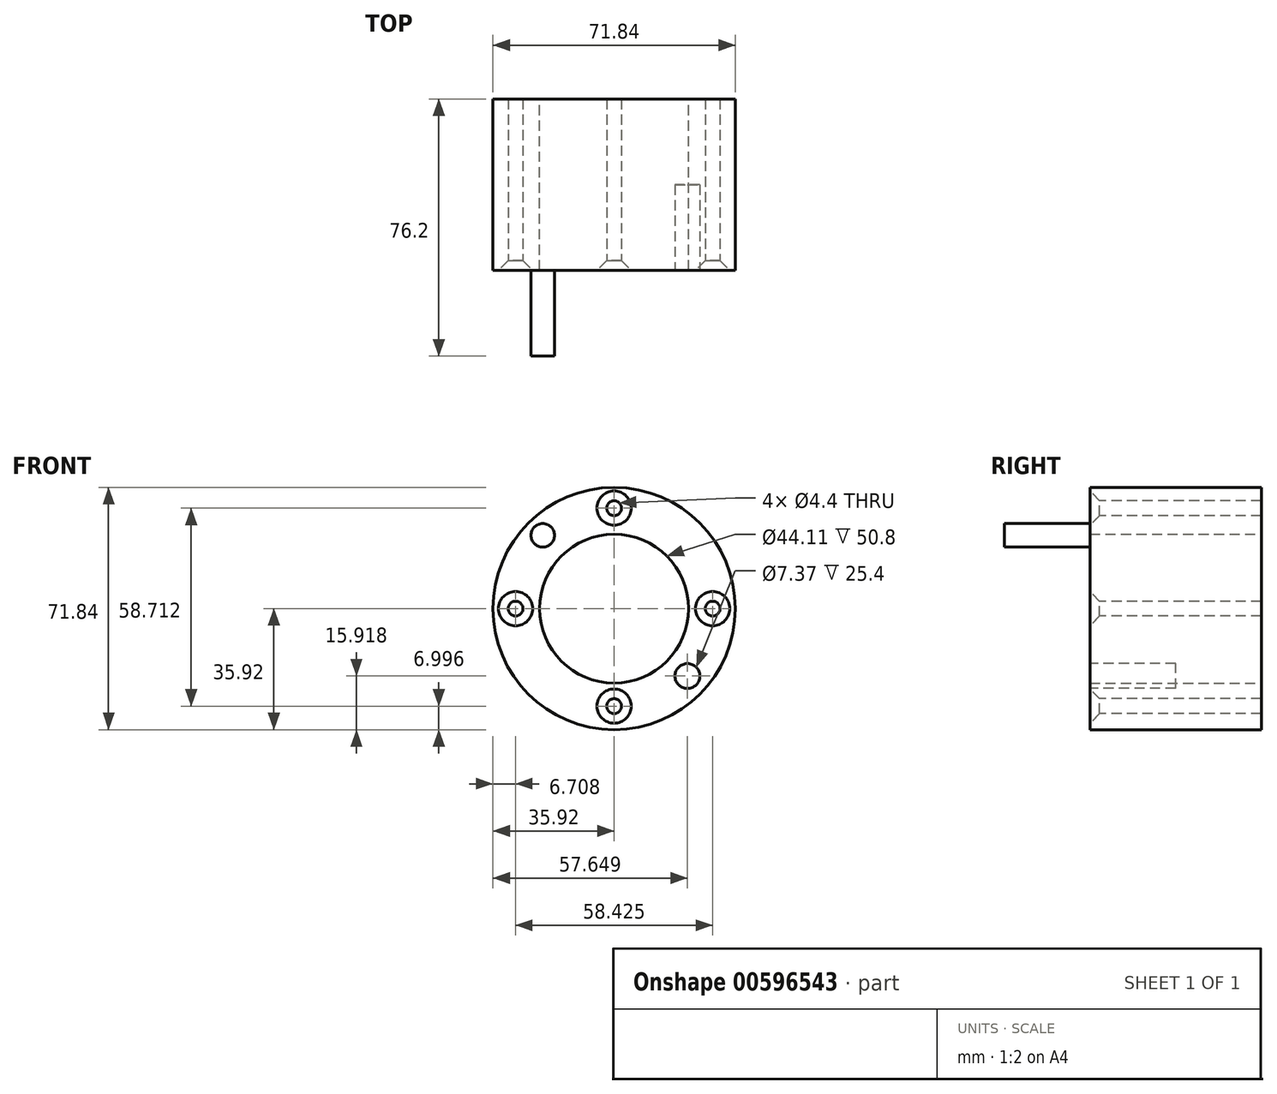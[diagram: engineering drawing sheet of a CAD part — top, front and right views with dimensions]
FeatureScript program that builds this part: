
annotation { "Feature Type Name" : "Feature", "Feature Type Description" : "" }
export const myFeature = defineFeature(function(context is Context, id is Id, definition is map)
    precondition{}
    {
        {
            var Q0;
            Q0=qCreatedBy(makeId("Front.planeOp"),FACE);
            var sketch = newSketch(context, id + "F0", { "sketchPlane" : qUnion([Q0])});
            skCircle(sketch, "E0", {"center": v(0, 0) * mm, "radius": 35.92 * mm});
            skCircle(sketch, "E1", {"center": v(0, 0) * mm, "radius": 22.06 * mm});
            skSolve(sketch);
        }
        {
            var Q0;
            Q0=makeQuery(id+"F0.imprint","IMPRINT",FACE,{"disambiguationData":[TD([[makeQuery(id+"F0.imprint","IMPRINT",EDGE,{"derivedFrom":sQuery(id+"F0.wireOp",EDGE,"E0")}),1.0]])]});
            extrude(context, id + "F1", {"entities" : qUnion([Q0]), "endBound" : BoundingType.SYMMETRIC, "depth" : 50.8 * mm, "offsetDistance" : 25.4 * mm});
        }
        {
            var Q0;
            Q0=makeQuery(id+"F1.opExtrude","CAP_FACE",FACE,{"disambiguationData":[OSD([sQuery(id+"F0.wireOp",EDGE,"E0"),sQuery(id+"F0.wireOp",EDGE,"E1")])],"isStart":false});
            var sketch = newSketch(context, id + "F2", { "sketchPlane" : qUnion([Q0])});
            skPoint(sketch, "E2", {"position": v(-29.21, 0) * mm});
            skPoint(sketch, "E3", {"position": v(0, 29.79) * mm});
            skPoint(sketch, "E4", {"position": v(29.21, 0) * mm});
            skPoint(sketch, "E5", {"position": v(0, -28.92) * mm});
            skSolve(sketch);
        }
        {
            var Q0;
            Q0=sQuery(id+"F2.wireOp",VERTEX,"E2");
            var Q1;
            Q1=sQuery(id+"F2.wireOp",VERTEX,"E3");
            var Q2;
            Q2=sQuery(id+"F2.wireOp",VERTEX,"E4");
            var Q3;
            Q3=sQuery(id+"F2.wireOp",VERTEX,"E5");
            var Q4;
            Q4=makeQuery(id+"F1.opExtrude","SWEPT_BODY",BODY,{"disambiguationData":[OSD([sQuery(id+"F0.wireOp",EDGE,"E0"),sQuery(id+"F0.wireOp",EDGE,"E1")])]});
            hole(context, id + "F3", {"style" : HoleStyle.C_SINK, "endStyle" : HoleEndStyle.THROUGH, "holeDiameter" : 4.4 * mm, "cSinkDiameter" : 10.16 * mm, "cSinkAngle" : 90 * degree, "majorDiameter" : 6.35 * mm, "isTappedThrough" : true, "tappedDepth" : 12.7 * mm, "tapClearance" : 3, "startFromSketch" : true, "locations" : qUnion([Q0, Q1, Q2, Q3]), "scope" : qUnion([Q4])});
        }
        {
            var Q0;
            Q0=makeQuery(id+"F1.opExtrude","CAP_FACE",FACE,{"disambiguationData":[OSD([sQuery(id+"F0.wireOp",EDGE,"E0"),sQuery(id+"F0.wireOp",EDGE,"E1")])],"isStart":false});
            var sketch = newSketch(context, id + "F4", { "sketchPlane" : qUnion([Q0])});
            skCircle(sketch, "E6", {"center": v(-21.15, 21.73) * mm, "radius": 3.48 * mm});
            skSolve(sketch);
        }
        {
            var Q0;
            Q0=makeQuery(id+"F4.imprint","IMPRINT",FACE,{"disambiguationData":[TD([[makeQuery(id+"F4.imprint","IMPRINT",EDGE,{"derivedFrom":sQuery(id+"F4.wireOp",EDGE,"E6")}),1.0]])]});
            extrude(context, id + "F5", {"entities" : qUnion([Q0]), "operationType" : NewBodyOperationType.ADD, "depth" : 25.4 * mm, "offsetDistance" : 25.4 * mm});
        }
        {
            var Q0;
            Q0=makeQuery(id+"F1.opExtrude","CAP_FACE",FACE,{"disambiguationData":[OSD([sQuery(id+"F0.wireOp",EDGE,"E0"),sQuery(id+"F0.wireOp",EDGE,"E1")])],"isStart":false});
            var sketch = newSketch(context, id + "F6", { "sketchPlane" : qUnion([Q0])});
            skCircle(sketch, "E7", {"center": v(21.73, -20) * mm, "radius": 3.69 * mm});
            skSolve(sketch);
        }
        {
            var Q0;
            Q0=makeQuery(id+"F6.imprint","IMPRINT",FACE,{"disambiguationData":[TD([[makeQuery(id+"F6.imprint","IMPRINT",EDGE,{"derivedFrom":sQuery(id+"F6.wireOp",EDGE,"E7")}),1.0]])]});
            extrude(context, id + "F7", {"entities" : qUnion([Q0]), "operationType" : NewBodyOperationType.REMOVE, "oppositeDirection" : true, "depth" : 25.4 * mm, "offsetDistance" : 25.4 * mm});
        }
    });
